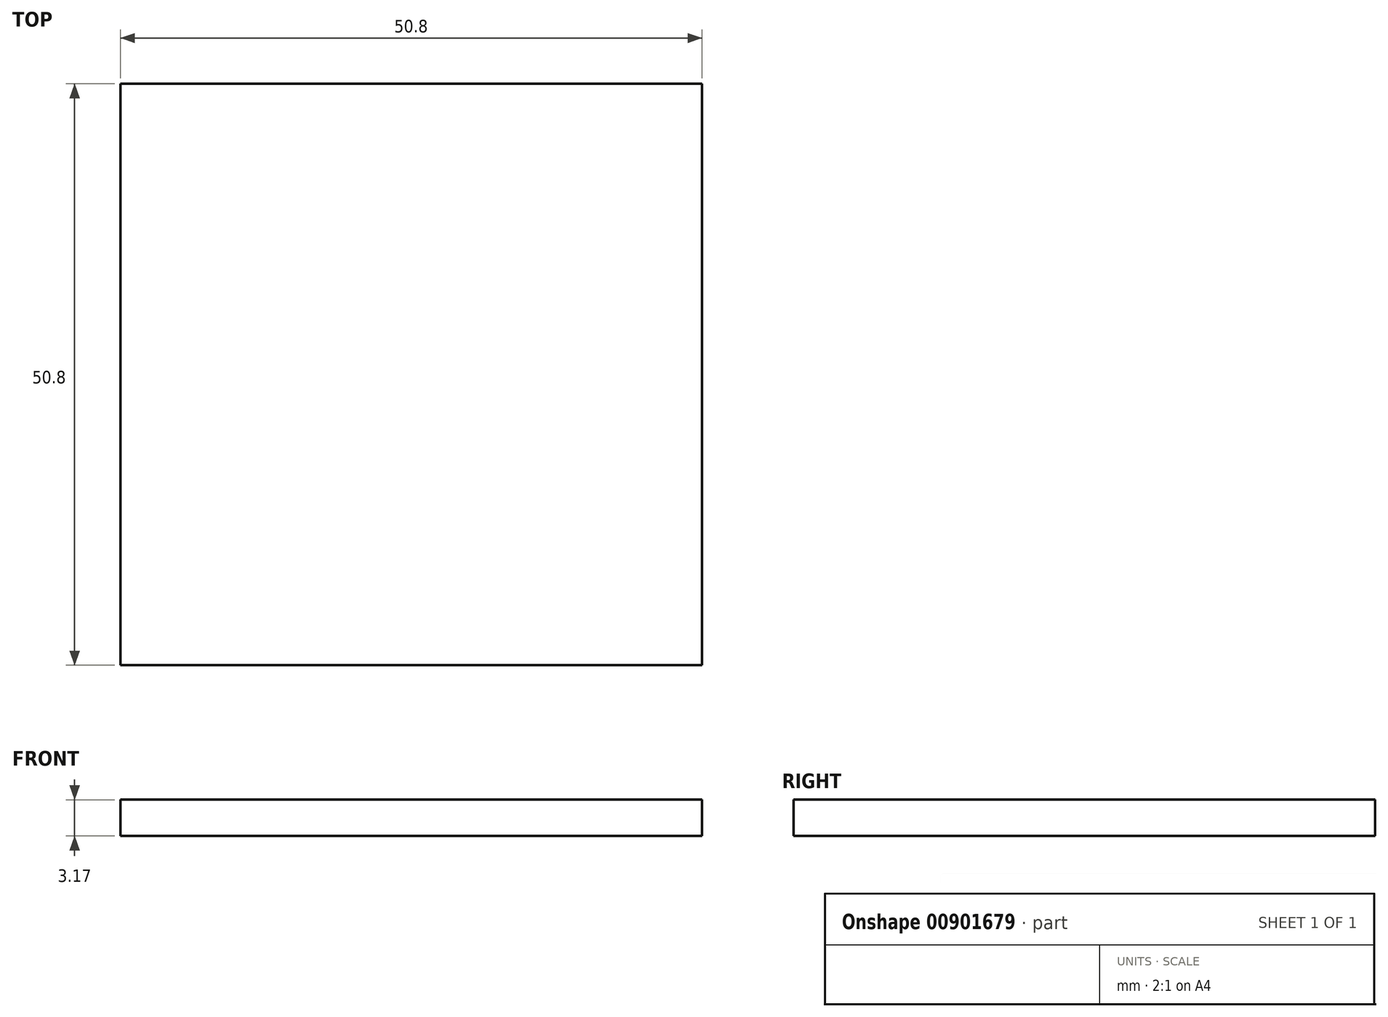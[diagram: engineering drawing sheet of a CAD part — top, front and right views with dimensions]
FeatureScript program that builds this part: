
annotation { "Feature Type Name" : "Feature", "Feature Type Description" : "" }
export const myFeature = defineFeature(function(context is Context, id is Id, definition is map)
    precondition{}
    {
        {
            var Q0;
            Q0=qCreatedBy(makeId("Top.planeOp"),FACE);
            var sketch = newSketch(context, id + "F0", { "sketchPlane" : qUnion([Q0])});
            skLineSegment(sketch, "E0.bottom", {"start": v(25.4, -25.4) * mm, "end": v(-25.4, -25.4) * mm});
            skLineSegment(sketch, "E0.top", {"start": v(25.4, 25.4) * mm, "end": v(-25.4, 25.4) * mm});
            skLineSegment(sketch, "E0.left", {"start": v(25.4, -25.4) * mm, "end": v(25.4, 25.4) * mm});
            skLineSegment(sketch, "E0.right", {"start": v(-25.4, -25.4) * mm, "end": v(-25.4, 25.4) * mm});
            skPoint(sketch, "E0.middle", {"position": v(0, 0) * mm});
            skSolve(sketch);
        }
        {
            var Q0;
            Q0 = qSketchRegion(id + "F0", true);
            extrude(context, id + "F1", {"entities" : qUnion([Q0]), "depth" : 3.17 * mm, "offsetDistance" : 25.4 * mm});
        }
    });
